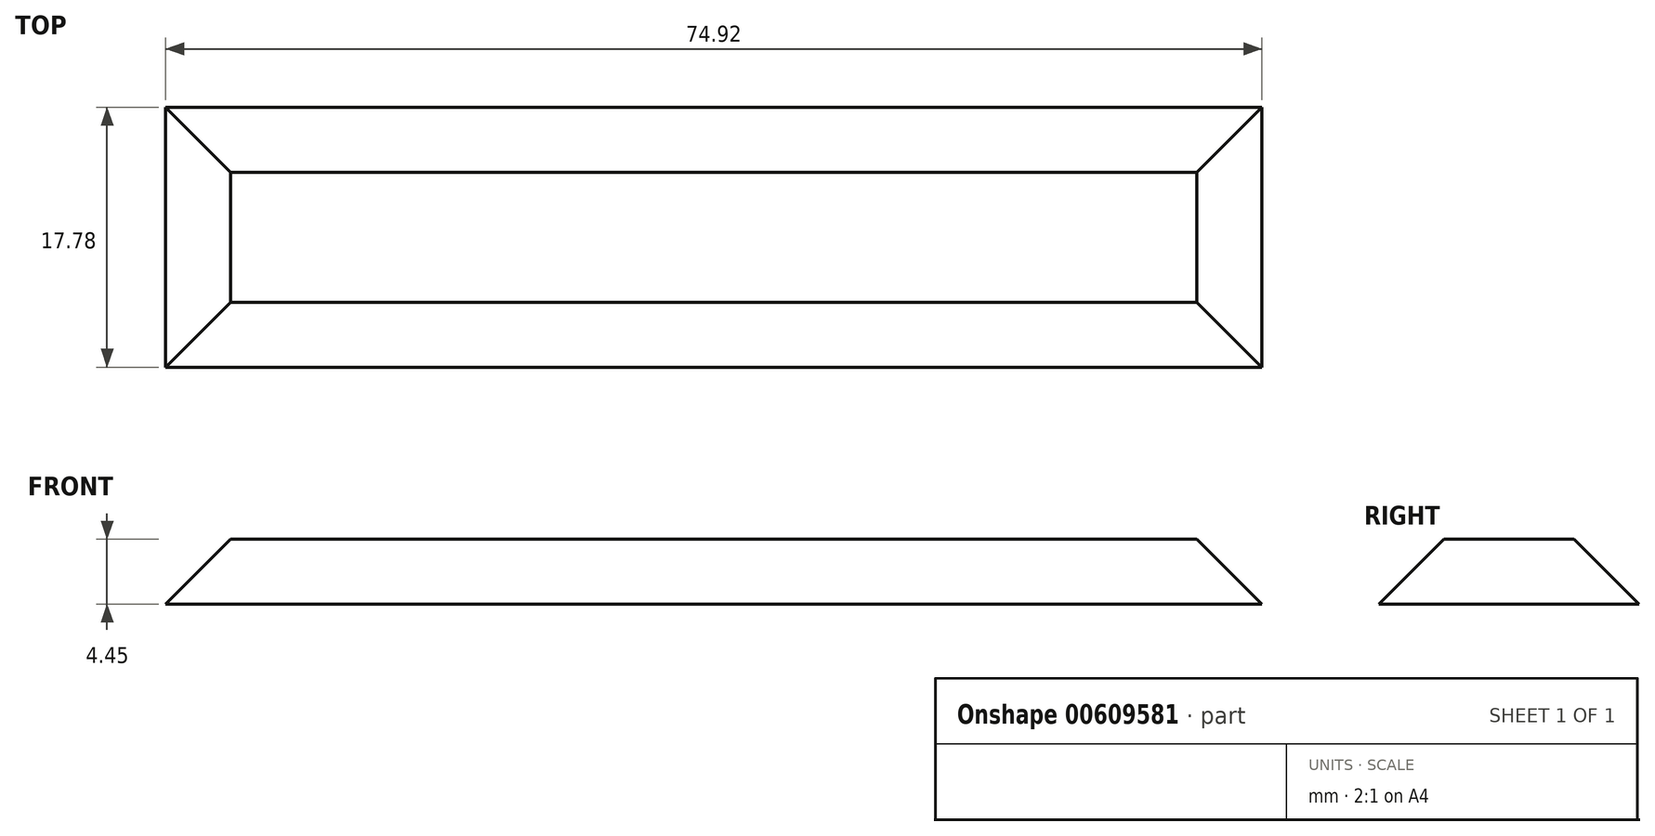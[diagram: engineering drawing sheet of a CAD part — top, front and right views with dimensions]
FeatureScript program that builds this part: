
annotation { "Feature Type Name" : "Feature", "Feature Type Description" : "" }
export const myFeature = defineFeature(function(context is Context, id is Id, definition is map)
    precondition{}
    {
        {
            var Q0;
            Q0=qCreatedBy(makeId("Top.planeOp"),FACE);
            var sketch = newSketch(context, id + "F0", { "sketchPlane" : qUnion([Q0])});
            skLineSegment(sketch, "E0.bottom", {"start": v(-38.1, 9.52) * mm, "end": v(38.1, 9.52) * mm});
            skLineSegment(sketch, "E0.top", {"start": v(-38.1, -9.53) * mm, "end": v(38.1, -9.53) * mm});
            skLineSegment(sketch, "E0.left", {"start": v(-38.1, 9.52) * mm, "end": v(-38.1, -9.53) * mm});
            skLineSegment(sketch, "E0.right", {"start": v(38.1, 9.52) * mm, "end": v(38.1, -9.53) * mm});
            skPoint(sketch, "E0.middle", {"position": v(0, 0) * mm});
            skSolve(sketch);
        }
        {
            var Q0;
            Q0 = qSketchRegion(id + "F2", true);
            var Q1;
            Q1=makeQuery(id+"F0.imprint","IMPRINT",FACE,{"disambiguationData":[TD([[makeQuery(id+"F0.imprint","IMPRINT",EDGE,{"derivedFrom":sQuery(id+"F0.wireOp",EDGE,"E0.bottom")}),-1.0]])]});
            extrude(context, id + "F1", {"entities" : qUnion([Q0, Q1]), "depth" : 4.44 * mm, "offsetDistance" : 25.4 * mm});
        }
        {
            var Q0;
            Q0=qCreatedBy(makeId("Top.planeOp"),FACE);
            var sketch = newSketch(context, id + "F2", { "sketchPlane" : qUnion([Q0])});
            skSolve(sketch);
        }
        {
            var Q0;
            Q0=makeQuery(id+"F1.opExtrude","CAP_EDGE",EDGE,{"disambiguationData":[OSD([sQuery(id+"F0.wireOp",EDGE,"E0.top")])],"isStart":false});
            var Q1;
            Q1=makeQuery(id+"F1.opExtrude","CAP_EDGE",EDGE,{"disambiguationData":[OSD([sQuery(id+"F0.wireOp",EDGE,"E0.left")])],"isStart":false});
            var Q2;
            Q2=makeQuery(id+"F1.opExtrude","CAP_EDGE",EDGE,{"disambiguationData":[OSD([sQuery(id+"F0.wireOp",EDGE,"E0.right")])],"isStart":false});
            var Q3;
            Q3=makeQuery(id+"F1.opExtrude","CAP_EDGE",EDGE,{"disambiguationData":[OSD([sQuery(id+"F0.wireOp",EDGE,"E0.bottom")])],"isStart":false});
            chamfer(context, id + "F3", {"entities" : qUnion([Q0, Q1, Q2, Q3]), "width" : 5.08 * mm, "tangentPropagation" : true});
        }
    });
